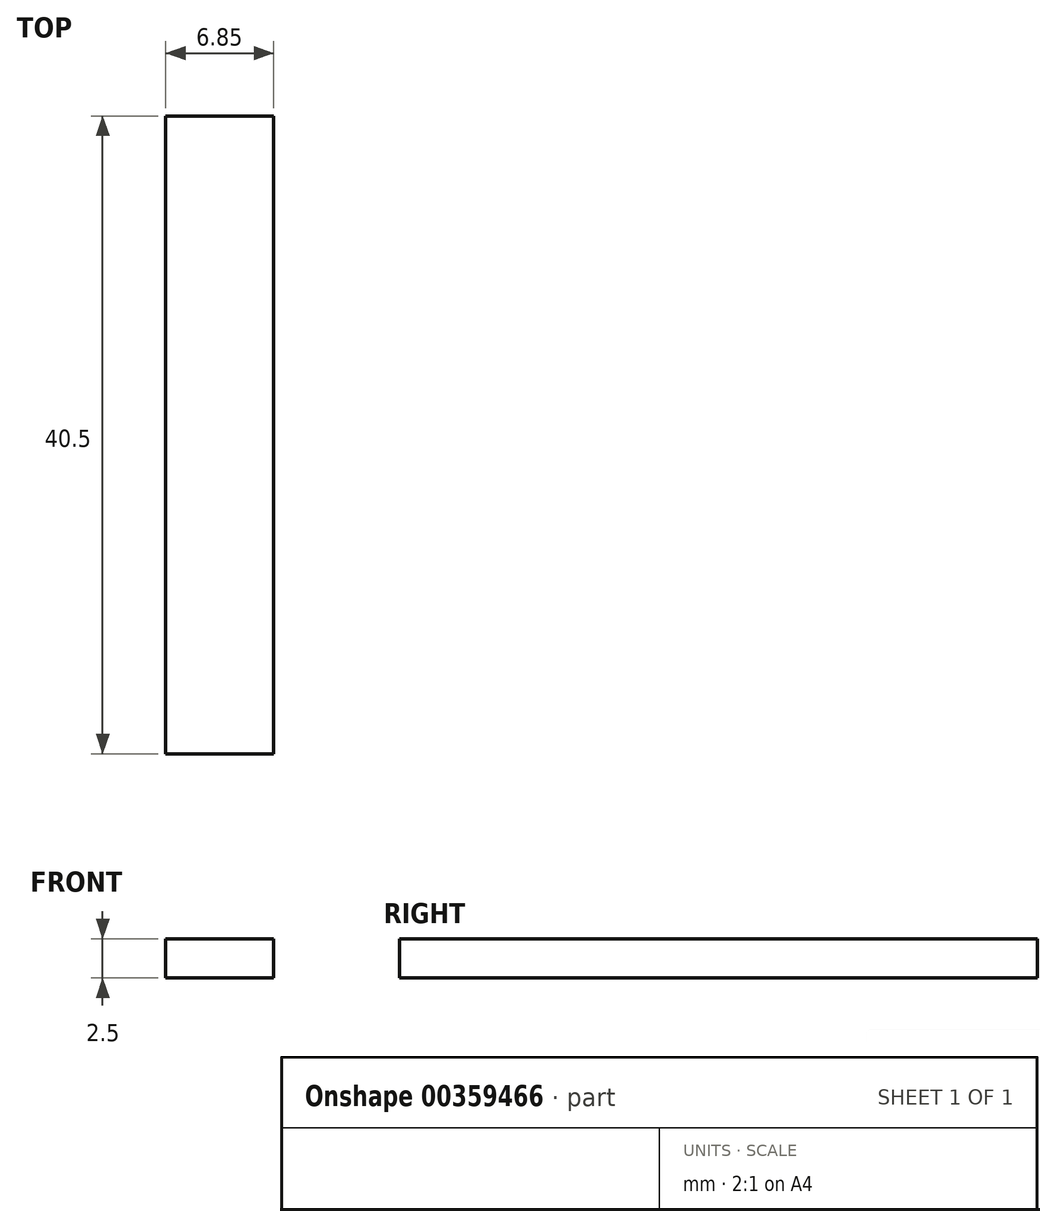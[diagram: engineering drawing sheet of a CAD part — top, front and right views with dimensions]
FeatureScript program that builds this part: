
annotation { "Feature Type Name" : "Feature", "Feature Type Description" : "" }
export const myFeature = defineFeature(function(context is Context, id is Id, definition is map)
    precondition{}
    {
        {
            var Q0;
            Q0=qCreatedBy(makeId("Top.planeOp"),FACE);
            var sketch = newSketch(context, id + "F0", { "sketchPlane" : qUnion([Q0])});
            skLineSegment(sketch, "E0.bottom", {"start": v(-6.12, -26.2) * mm, "end": v(0.73, -26.2) * mm});
            skLineSegment(sketch, "E0.top", {"start": v(-6.12, 14.3) * mm, "end": v(0.73, 14.3) * mm});
            skLineSegment(sketch, "E0.left", {"start": v(-6.12, -26.2) * mm, "end": v(-6.12, 14.3) * mm});
            skLineSegment(sketch, "E0.right", {"start": v(0.73, -26.2) * mm, "end": v(0.73, 14.3) * mm});
            skSolve(sketch);
        }
        {
            var Q0;
            Q0=makeQuery(id+"F0.imprint","IMPRINT",FACE,{"disambiguationData":[TD([[makeQuery(id+"F0.imprint","IMPRINT",EDGE,{"derivedFrom":sQuery(id+"F0.wireOp",EDGE,"E0.bottom")}),1.0]])]});
            extrude(context, id + "F1", {"entities" : qUnion([Q0]), "depth" : 2.5 * mm});
        }
    });
